# Revit family: VIESSMANN - Vitocal 200-G Pro
name_source: partatom
category: Wyposażenie mechaniczne
revit_build: Autodesk Revit 2017 (Build: 20160720_1515(x64)
units: mm (PartAtom-declared; Revit-internal decimal feet)

## family parameters
Numer OmniClass = 23.75.10.21.17
Oparty na płaszczyźnie roboczej = Nie
Punkt obliczania pomieszczeń = Nie
Tnij formami wycięć po wczytaniu = Nie
Typ części = Normalny
Tytuł OmniClass = Water-Source Heat Pumps
Współdzielony = Nie
Wymiar okrągłego złącza = Użyj średnicy
Zawsze pionowo = Tak

## types (2) — shared parameters
Autor = www.archispace.pl
Cos Phi sprężarki przy maks. mocy w B15/W35 = 0.72
Czynnik chłodniczy = R410A
Częstotliwość = 50 Hz
Dopuszczalne ciśnienie robocze. Strona niskociśnieniowa = 1.8 MPa
Dopuszczalne ciśnienie robocze. Strona wysokociśnieniowa = 4.5 MPa
Długość całkowita = 1753 mm  [stored 5.75131 ft]
Liczba biegunów = 3
Liczba obiegów chłodniczych = 1
Liczba sprężarek = 2
Model = Solankowa pompa ciepła Vitocal 200-G PRO 80kW / Brine-water heat pump Vitocal 200-G PRO 80kW
Napięcie znamionowe = 400 V
Obieg pierwotny od strony parownika (Victaulic) = 2½" (DN 65)
Obieg pierwotny od strony zestawu przyłączy (kołnierz) = DN 65/PN 10
Obieg pierwotny. Dop. ciśnienie robocze = 1.0 MPa
Obieg pierwotny. Ochrona przed zamarzaniem/temperatura początku krystalizacji (zalecany czynnik chłodzący Tyfocor) = -12 °C
Obieg pierwotny. Opór przepływu przy minimalnym przepływie objętościowym = 20.0 kPa
Obieg pierwotny. Różnica temperatur = 3 °C
Obieg wtórny od strony skraplacza (Victaulic) = 2½" (DN 65)
Obieg wtórny od strony zestawu przyłączy (kołnierz) = DN 65/PN 10
Obieg wtórny. Dop. ciśnienie robocze = 1.0 MPa
Obieg wtórny. Maks. temperatura na zasilaniu na wlocie z obiegu pierwotnego B +5°C = 60 °C
Obieg wtórny. Maks. temperatura na zasilaniu na wlocie z obiegu pierwotnego B +8°C = 0 °C
Obieg wtórny. Maks. temperatura na zasilaniu na wlocie z obiegu pierwotnego B 0°C = 55 °C
Obieg wtórny. Opór przepływu przy minimalnym przepływie objętościowym = 4.0 kPa
Obieg wtórny. Opór przepływu przy znamionowym przepływie objętościowym (całkowita strata ciśnienia skraplacza z przyłączami) = 6.0 kPa
Obieg wtórny. Różnica temperatur = 5 °C
Opis = 2-stopniowe pompy ciepła solanka/woda z napędem elektrycznym do stosowania w jedno- lub dwusystemowych instalacjach grzewczych.
Producent = Viessmann Sp. z o.o.
Rodzaj sprężarki = Scroll - całkowicie hermetyczna
Stopień ochrony = IP54
System rozruchowy = Moduł łagodnego rozruchu
Szerokość całkowita = 800 mm  [stored 2.62467 ft]
URL = https://www.viessmann-projektant.pl
Viessmann Kolor 1 = Viessmann Kolor 1
Viessmann Kolor 4 = Viessmann Kolor 4
Współczynnik mocy = 0.72
Wysokość całkowita = 1457 mm  [stored 4.78018 ft]
Zasilanie elektryczne (V/ph/Hz) = 3LNPE/400 V/50 Hz
etas LT = 189
Średnica odejścia = 65 mm  [stored 0.213255 ft]

## per-type parameters (varying)
- BW 202.A080. Solanka/woda (B0/W35): Całkowity maksymalny pobór mocy=26.2 kW; Całkowity prąd rozruchowy (stopniowo)=102 A; Ilość oleju=6.6 L; Maks. prąd roboczy=45 A; Maksymalne dopuszczalne zabezpieczenie zasilania przez inwestora=63 A; Masa całkowita (urządzenie podstawowe bez opcjonalnej obudowy)=452.00 kg; Największe wewnętrzne zabezpieczenie pompy ciepła (charakterystyka zadziałania "C")=32 A; Natężenie znamionowe sprężarek (łącznie)=33 A; Obciążenie pozorne=36389 W; Obieg pierwotny. Minimalny przepływ objętościowy=12.4 m³/h; Obieg pierwotny. Opór przepływu przy znamionowym przepływie objętościowym (całkowita strata ciśnienia skraplacza z przyłączami)=26.0 kPa; Obieg pierwotny. Pojemność wymiennika ciepła (solanka)=9.1 L; Obieg pierwotny. Znamionowy przepływ objętościowy (wartość zalecana do projektowania)=17.7 m³/h; Obieg wtórny. Minimalny przepływ objętościowy=9.1 m³/h; Obieg wtórny. Pojemność wymiennika ciepła (woda)=13.1 L; Obieg wtórny. Znamionowy przepływ objętościowy (wartość zalecana do projektowania)=13.1 m³/h; Pobór mocy elektrycznej=16.2 kW; Poziom mocy akustycznej=79 dB(A); Prąd rozruchowy na sprężarkę (sprężarka 1/sprężarka 2)=79,0/79,0; SCOP LT=4.93; SCOP MT=3.68; Stopień efektywności ε (COP)=4.66; Wielkość napełnienia (wytyczna)=9.90 kg; Wydajność chłodnicza=59.2 kW; Znamionowa moc grzewcza=75.4 kW; etas MT=139
- BW 202.A100. Solanka/woda (B0/W35): Całkowity maksymalny pobór mocy=35.0 kW; Całkowity prąd rozruchowy (stopniowo)=134 A; Ilość oleju=10.3 L; Maks. prąd roboczy=60 A; Maksymalne dopuszczalne zabezpieczenie zasilania przez inwestora=80 A; Masa całkowita (urządzenie podstawowe bez opcjonalnej obudowy)=538.00 kg; Największe wewnętrzne zabezpieczenie pompy ciepła (charakterystyka zadziałania "C")=50 A; Natężenie znamionowe sprężarek (łącznie)=43 A; Obciążenie pozorne=48611 W; Obieg pierwotny. Minimalny przepływ objętościowy=16.5 m³/h; Obieg pierwotny. Opór przepływu przy znamionowym przepływie objętościowym (całkowita strata ciśnienia skraplacza z przyłączami)=27.0 kPa; Obieg pierwotny. Pojemność wymiennika ciepła (solanka)=12.1 L; Obieg pierwotny. Znamionowy przepływ objętościowy (wartość zalecana do projektowania)=23.5 m³/h; Obieg wtórny. Minimalny przepływ objętościowy=12.2 m³/h; Obieg wtórny. Pojemność wymiennika ciepła (woda)=17.2 L; Obieg wtórny. Znamionowy przepływ objętościowy (wartość zalecana do projektowania)=17.4 m³/h; Pobór mocy elektrycznej=21.7 kW; Poziom mocy akustycznej=84 dB(A); Prąd rozruchowy na sprężarkę (sprężarka 1/sprężarka 2)=98,0/107,5; SCOP LT=4.92; SCOP MT=3.7; Stopień efektywności ε (COP)=4.65; Wielkość napełnienia (wytyczna)=13.50 kg; Wydajność chłodnicza=79.3 kW; Znamionowa moc grzewcza=101.0 kW; etas MT=140

note: [stored X ft] marks values corroborated as IEEE doubles in the binary element streams (Revit-internal decimal feet)

## geometry (parser evidence)
native form markers: Sweep x3
no freeform markers — native parametric forms only
